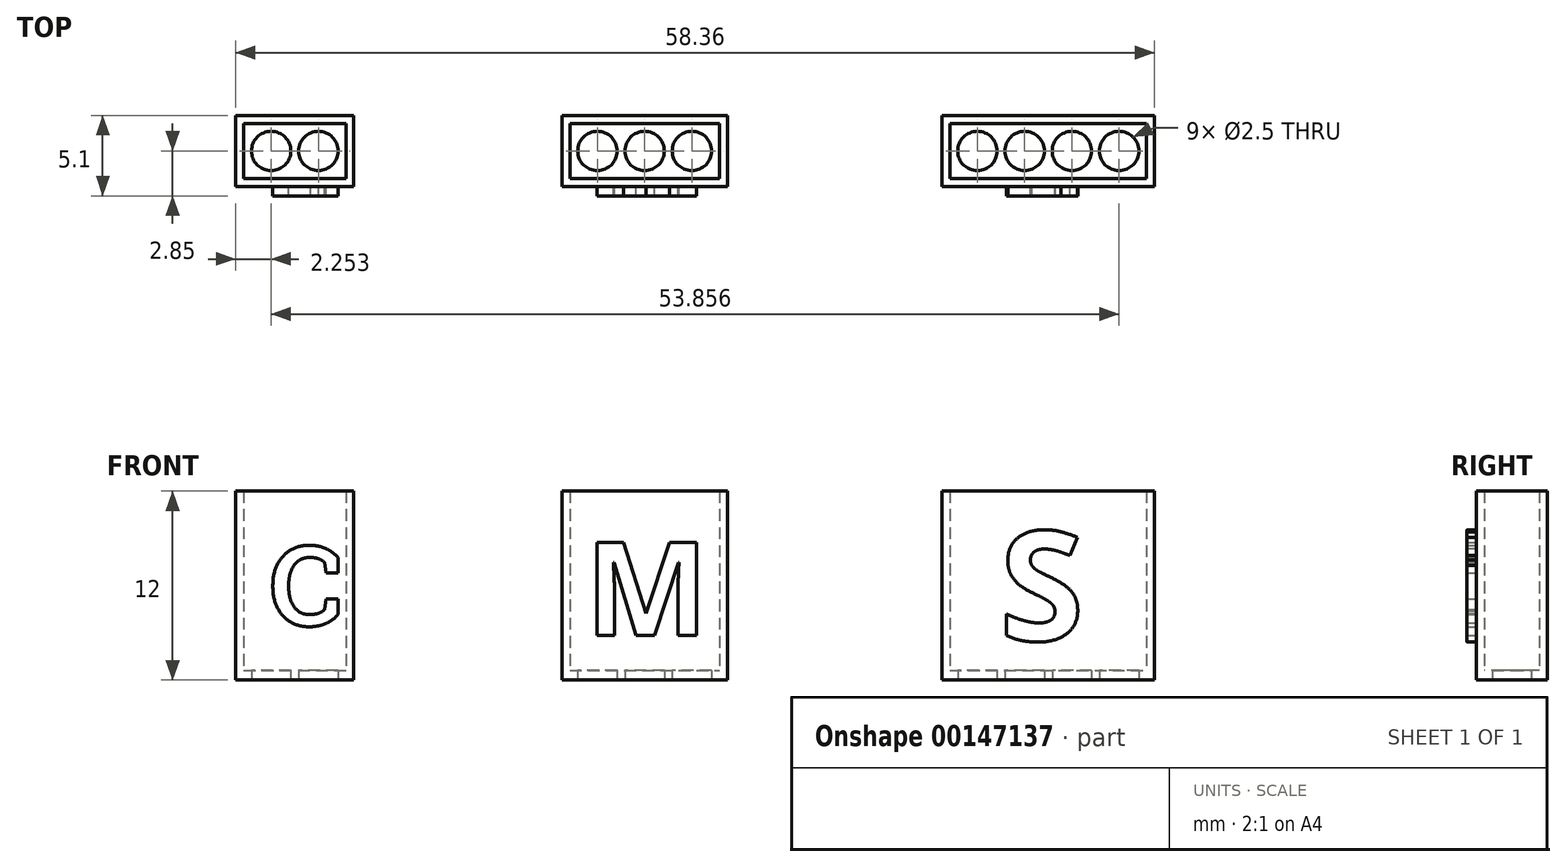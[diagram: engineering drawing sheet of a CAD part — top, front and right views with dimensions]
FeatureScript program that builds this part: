
annotation { "Feature Type Name" : "Feature", "Feature Type Description" : "" }
export const myFeature = defineFeature(function(context is Context, id is Id, definition is map)
    precondition{}
    {
        {
            var Q0;
            Q0=qCreatedBy(makeId("Top.planeOp"),FACE);
            var sketch = newSketch(context, id + "F0", { "sketchPlane" : qUnion([Q0])});
            skLineSegment(sketch, "E0.bottom", {"start": v(-50.7, -0.5) * mm, "end": v(-44.2, -0.5) * mm});
            skLineSegment(sketch, "E0.top", {"start": v(-50.7, -4) * mm, "end": v(-44.2, -4) * mm});
            skLineSegment(sketch, "E0.left", {"start": v(-50.7, -0.5) * mm, "end": v(-50.7, -4) * mm});
            skLineSegment(sketch, "E0.right", {"start": v(-44.2, -0.5) * mm, "end": v(-44.2, -4) * mm});
            skCircle(sketch, "E1", {"center": v(-48.95, -2.25) * mm, "radius": 1.25 * mm});
            skCircle(sketch, "E2", {"center": v(-45.95, -2.25) * mm, "radius": 1.25 * mm});
            skLineSegment(sketch, "E3.bottom", {"start": v(-51.2, 0) * mm, "end": v(-43.7, 0) * mm});
            skLineSegment(sketch, "E3.top", {"start": v(-51.2, -4.5) * mm, "end": v(-43.7, -4.5) * mm});
            skLineSegment(sketch, "E3.left", {"start": v(-51.2, 0) * mm, "end": v(-51.2, -4.5) * mm});
            skLineSegment(sketch, "E3.right", {"start": v(-43.7, 0) * mm, "end": v(-43.7, -4.5) * mm});
            skLineSegment(sketch, "E4.bottom", {"start": v(-29.98, -0.5) * mm, "end": v(-20.48, -0.5) * mm});
            skLineSegment(sketch, "E4.top", {"start": v(-29.98, -4) * mm, "end": v(-20.48, -4) * mm});
            skLineSegment(sketch, "E4.left", {"start": v(-29.98, -0.5) * mm, "end": v(-29.98, -4) * mm});
            skLineSegment(sketch, "E4.right", {"start": v(-20.48, -0.5) * mm, "end": v(-20.48, -4) * mm});
            skCircle(sketch, "E5", {"center": v(-28.23, -2.25) * mm, "radius": 1.25 * mm});
            skCircle(sketch, "E6", {"center": v(-25.23, -2.25) * mm, "radius": 1.25 * mm});
            skLineSegment(sketch, "E7.bottom", {"start": v(-30.48, 0) * mm, "end": v(-19.98, 0) * mm});
            skLineSegment(sketch, "E7.top", {"start": v(-30.48, -4.5) * mm, "end": v(-19.98, -4.5) * mm});
            skLineSegment(sketch, "E7.left", {"start": v(-30.48, 0) * mm, "end": v(-30.48, -4.5) * mm});
            skLineSegment(sketch, "E7.right", {"start": v(-19.98, 0) * mm, "end": v(-19.98, -4.5) * mm});
            skLineSegment(sketch, "E8.bottom", {"start": v(-5.84, -0.5) * mm, "end": v(6.66, -0.5) * mm});
            skLineSegment(sketch, "E8.top", {"start": v(-5.84, -4) * mm, "end": v(6.66, -4) * mm});
            skLineSegment(sketch, "E8.left", {"start": v(-5.84, -0.5) * mm, "end": v(-5.84, -4) * mm});
            skLineSegment(sketch, "E8.right", {"start": v(6.66, -0.5) * mm, "end": v(6.66, -4) * mm});
            skCircle(sketch, "E9", {"center": v(-4.1, -2.25) * mm, "radius": 1.25 * mm});
            skCircle(sketch, "E10", {"center": v(-1.1, -2.25) * mm, "radius": 1.25 * mm});
            skLineSegment(sketch, "E11.bottom", {"start": v(-6.34, 0) * mm, "end": v(7.16, 0) * mm});
            skLineSegment(sketch, "E11.top", {"start": v(-6.34, -4.5) * mm, "end": v(7.16, -4.5) * mm});
            skLineSegment(sketch, "E11.left", {"start": v(-6.34, 0) * mm, "end": v(-6.34, -4.5) * mm});
            skLineSegment(sketch, "E11.right", {"start": v(7.16, 0) * mm, "end": v(7.16, -4.5) * mm});
            skCircle(sketch, "E12", {"center": v(-22.23, -2.25) * mm, "radius": 1.25 * mm});
            skCircle(sketch, "E13", {"center": v(1.9, -2.25) * mm, "radius": 1.25 * mm});
            skCircle(sketch, "E14", {"center": v(4.9, -2.25) * mm, "radius": 1.25 * mm});
            skSolve(sketch);
        }
        {
            var Q0;
            Q0=makeQuery(id+"F0.imprint","IMPRINT",FACE,{"disambiguationData":[TD([[makeQuery(id+"F0.imprint","IMPRINT",EDGE,{"derivedFrom":sQuery(id+"F0.wireOp",EDGE,"E0.bottom")}),-1.0]])]});
            var Q1;
            Q1=makeQuery(id+"F0.imprint","IMPRINT",FACE,{"disambiguationData":[TD([[makeQuery(id+"F0.imprint","IMPRINT",EDGE,{"derivedFrom":sQuery(id+"F0.wireOp",EDGE,"E4.bottom")}),-1.0]])]});
            var Q2;
            Q2=makeQuery(id+"F0.imprint","IMPRINT",FACE,{"disambiguationData":[TD([[makeQuery(id+"F0.imprint","IMPRINT",EDGE,{"derivedFrom":sQuery(id+"F0.wireOp",EDGE,"E8.bottom")}),-1.0]])]});
            extrude(context, id + "F1", {"entities" : qUnion([Q0, Q1, Q2]), "depth" : .6 * mm});
        }
        {
            var Q0;
            Q0=makeQuery(id+"F0.imprint","IMPRINT",FACE,{"disambiguationData":[TD([[makeQuery(id+"F0.imprint","IMPRINT",EDGE,{"derivedFrom":sQuery(id+"F0.wireOp",EDGE,"E0.bottom")}),1.0]])]});
            var Q1;
            Q1=makeQuery(id+"F0.imprint","IMPRINT",FACE,{"disambiguationData":[TD([[makeQuery(id+"F0.imprint","IMPRINT",EDGE,{"derivedFrom":sQuery(id+"F0.wireOp",EDGE,"E4.bottom")}),1.0]])]});
            var Q2;
            Q2=makeQuery(id+"F0.imprint","IMPRINT",FACE,{"disambiguationData":[TD([[makeQuery(id+"F0.imprint","IMPRINT",EDGE,{"derivedFrom":sQuery(id+"F0.wireOp",EDGE,"E8.bottom")}),1.0]])]});
            extrude(context, id + "F2", {"entities" : qUnion([Q0, Q1, Q2]), "operationType" : NewBodyOperationType.ADD, "depth" : 12 * mm});
        }
        {
            var Q0;
            Q0=makeQuery(id+"F2.opExtrude","SWEPT_FACE",FACE,{"disambiguationData":[OSD([sQuery(id+"F0.wireOp",EDGE,"E3.top")])]});
            var sketch = newSketch(context, id + "F3", { "sketchPlane" : qUnion([Q0])});
            skText(sketch, "E15", { "text": "C", "fontName": "RobotoSlab-Bold.ttf"});
            const initialGuessF3  = {"E15": [-0.04902, 0.00345, 1, 0, 0.0051]};
            skSetInitialGuess(sketch, initialGuessF3);
            skSolve(sketch);
        }
        {
            var Q0;
            Q0=makeQuery(id+"F3.imprint","IMPRINT",FACE,{"disambiguationData":[TD([[makeQuery(id+"F3.imprint","IMPRINT",EDGE,{"derivedFrom":sQuery(id+"F3.wireOp",EDGE,"E15.sketch_text.stroke-0")}),-1.0]])]});
            extrude(context, id + "F4", {"entities" : qUnion([Q0]), "operationType" : NewBodyOperationType.ADD, "depth" : .6 * mm});
        }
        {
            var Q0;
            Q0=makeQuery(id+"F2.opExtrude","SWEPT_FACE",FACE,{"disambiguationData":[OSD([sQuery(id+"F0.wireOp",EDGE,"E7.top")])]});
            var sketch = newSketch(context, id + "F5", { "sketchPlane" : qUnion([Q0])});
            skText(sketch, "E16", { "text": "M", "fontName": "OpenSans-Bold.ttf"});
            const initialGuessF5  = {"E16": [-0.029, 0.00284, 1, 0, 0.00596]};
            skSetInitialGuess(sketch, initialGuessF5);
            skSolve(sketch);
        }
        {
            var Q0;
            Q0 = qSketchRegion(id + "F5", true);
            extrude(context, id + "F6", {"entities" : qUnion([Q0]), "operationType" : NewBodyOperationType.ADD, "depth" : .6 * mm});
        }
        {
            var Q0;
            Q0=makeQuery(id+"F2.opExtrude","SWEPT_FACE",FACE,{"disambiguationData":[OSD([sQuery(id+"F0.wireOp",EDGE,"E11.top")])]});
            var sketch = newSketch(context, id + "F7", { "sketchPlane" : qUnion([Q0])});
            skText(sketch, "E17", { "text": "S", "fontName": "OpenSans-Bold.ttf"});
            const initialGuessF7  = {"E17": [-0.00269, 0.0025, 1, 0, 0.007]};
            skSetInitialGuess(sketch, initialGuessF7);
            skSolve(sketch);
        }
        {
            var Q0;
            Q0 = qSketchRegion(id + "F7", true);
            extrude(context, id + "F8", {"entities" : qUnion([Q0]), "operationType" : NewBodyOperationType.ADD, "depth" : .6 * mm});
        }
    });
